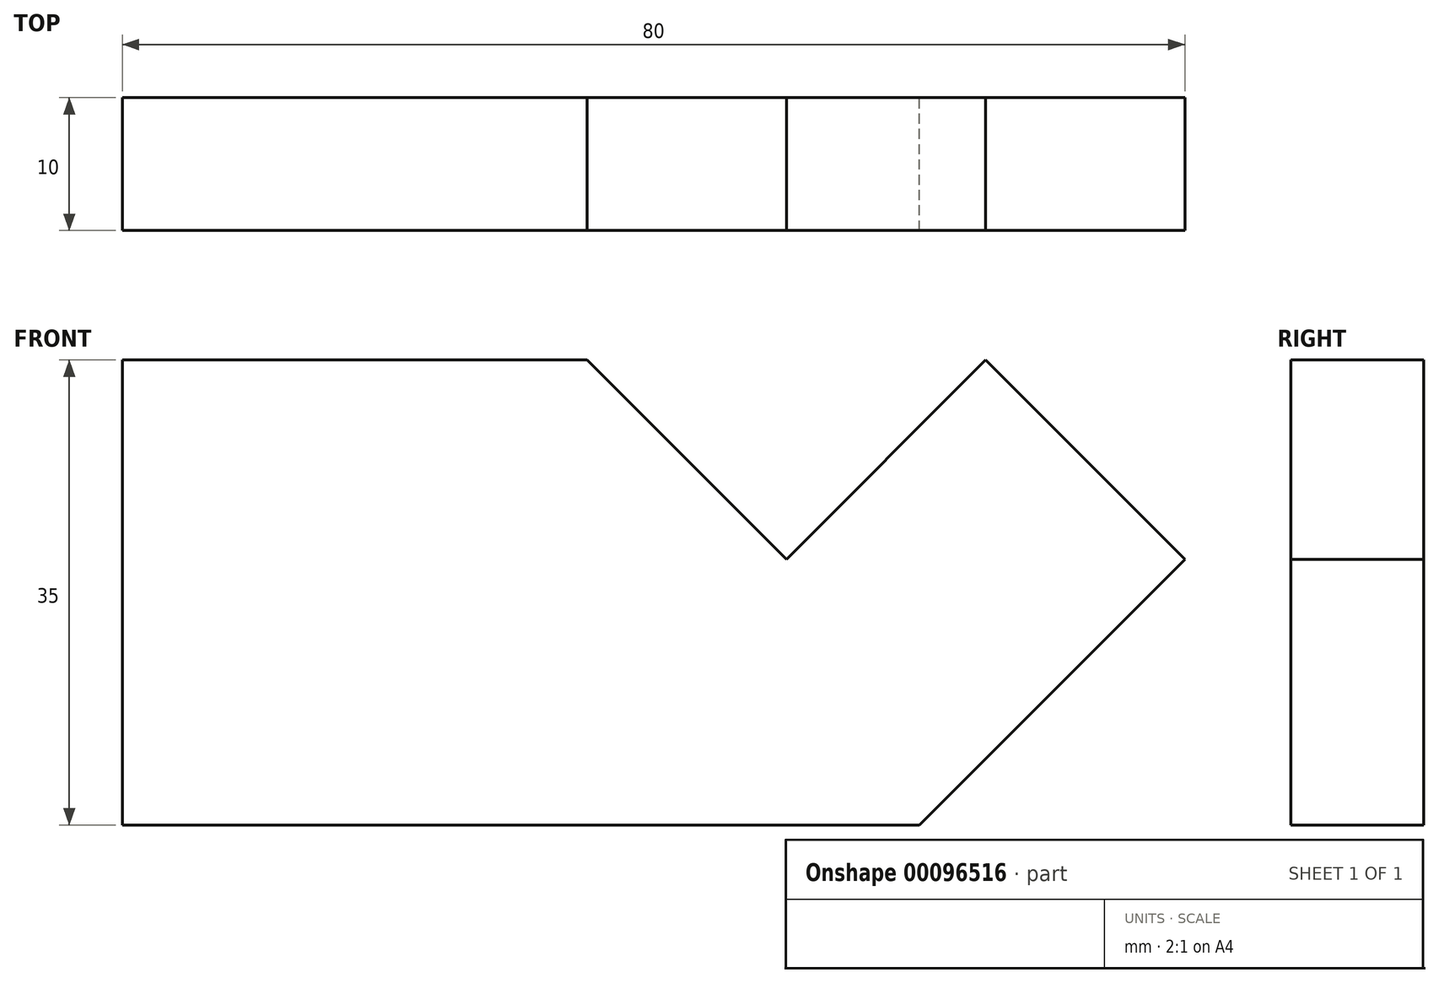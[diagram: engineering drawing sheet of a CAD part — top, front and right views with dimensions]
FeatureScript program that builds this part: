
annotation { "Feature Type Name" : "Feature", "Feature Type Description" : "" }
export const myFeature = defineFeature(function(context is Context, id is Id, definition is map)
    precondition{}
    {
        {
            var Q0;
            Q0=qCreatedBy(makeId("Front.planeOp"),FACE);
            var sketch = newSketch(context, id + "F0", { "sketchPlane" : qUnion([Q0])});
            skLineSegment(sketch, "E0", {"start": v(0, 0) * mm, "end": v(0, 35) * mm});
            skLineSegment(sketch, "E1", {"start": v(0, 0) * mm, "end": v(60, 0) * mm});
            skLineSegment(sketch, "E2", {"start": v(60, 0) * mm, "end": v(80, 20) * mm});
            skLineSegment(sketch, "E3", {"start": v(0, 35) * mm, "end": v(35, 35) * mm});
            skLineSegment(sketch, "E4", {"start": v(80, 20) * mm, "end": v(65, 35) * mm});
            skLineSegment(sketch, "E5", {"start": v(65, 35) * mm, "end": v(50, 20) * mm});
            skLineSegment(sketch, "E6", {"start": v(50, 20) * mm, "end": v(35, 35) * mm});
            skSolve(sketch);
        }
        {
            var Q0;
            Q0 = qSketchRegion(id + "F0", true);
            extrude(context, id + "F1", {"entities" : qUnion([Q0]), "depth" : 10 * mm});
        }
    });
